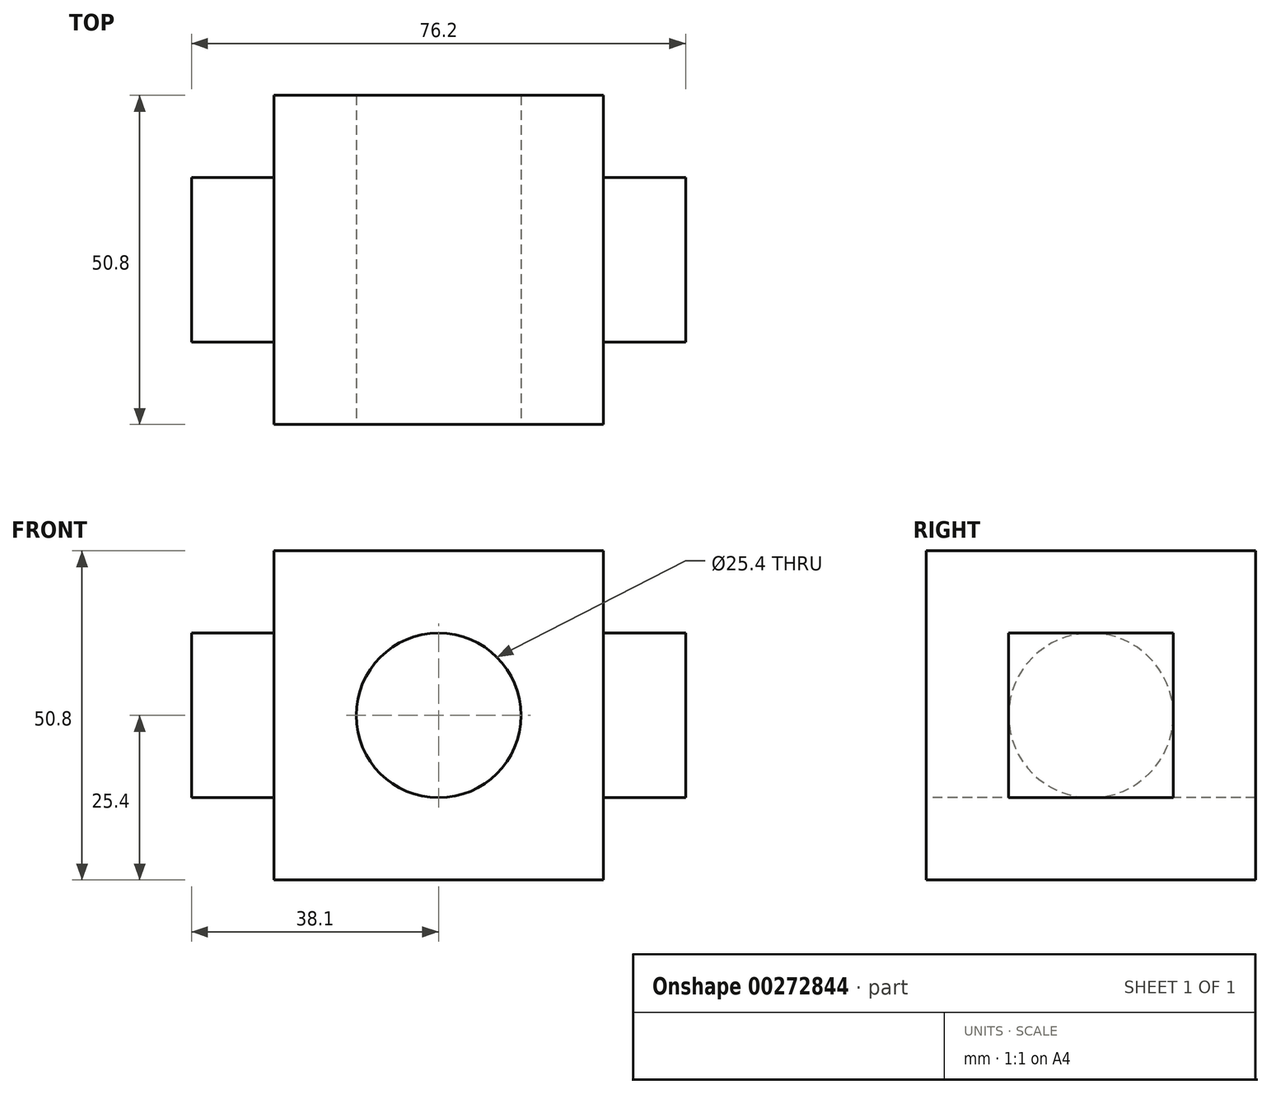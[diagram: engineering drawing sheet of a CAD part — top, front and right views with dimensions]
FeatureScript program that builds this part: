
annotation { "Feature Type Name" : "Feature", "Feature Type Description" : "" }
export const myFeature = defineFeature(function(context is Context, id is Id, definition is map)
    precondition{}
    {
        {
            var Q0;
            Q0=qCreatedBy(makeId("Front.planeOp"),FACE);
            var sketch = newSketch(context, id + "F0", { "sketchPlane" : qUnion([Q0])});
            skLineSegment(sketch, "E0", {"start": v(0, 0) * mm, "end": v(-50.8, 0) * mm});
            skLineSegment(sketch, "E1", {"start": v(-50.8, 0) * mm, "end": v(-50.8, 50.8) * mm});
            skLineSegment(sketch, "E2", {"start": v(-50.8, 50.8) * mm, "end": v(0, 50.8) * mm});
            skLineSegment(sketch, "E3", {"start": v(0, 50.8) * mm, "end": v(0, 0) * mm});
            skSolve(sketch);
        }
        {
            var Q0;
            Q0=makeQuery(id+"F0.imprint","IMPRINT",FACE,{"disambiguationData":[TD([[makeQuery(id+"F0.imprint","IMPRINT",EDGE,{"derivedFrom":sQuery(id+"F0.wireOp",EDGE,"E0")}),-1.0]])]});
            extrude(context, id + "F1", {"entities" : qUnion([Q0]), "depth" : 50.8 * mm});
        }
        {
            var Q0;
            Q0=makeQuery(id+"F1.opExtrude","CAP_FACE",FACE,{"disambiguationData":[OSD([sQuery(id+"F0.wireOp",EDGE,"E0"),sQuery(id+"F0.wireOp",EDGE,"E1"),sQuery(id+"F0.wireOp",EDGE,"E2"),sQuery(id+"F0.wireOp",EDGE,"E3")])],"isStart":false});
            var sketch = newSketch(context, id + "F2", { "sketchPlane" : qUnion([Q0])});
            skCircle(sketch, "E4", {"center": v(-25.4, 25.4) * mm, "radius": 12.7 * mm});
            skSolve(sketch);
        }
        {
            var Q0;
            Q0=makeQuery(id+"F2.imprint","IMPRINT",FACE,{"disambiguationData":[TD([[makeQuery(id+"F2.imprint","IMPRINT",EDGE,{"derivedFrom":sQuery(id+"F2.wireOp",EDGE,"E4")}),1.0]])]});
            extrude(context, id + "F3", {"entities" : qUnion([Q0]), "operationType" : NewBodyOperationType.REMOVE, "oppositeDirection" : true, "depth" : 50.8 * mm});
        }
        {
            var Q0;
            Q0=makeQuery(id+"F1.opExtrude","SWEPT_FACE",FACE,{"disambiguationData":[OSD([sQuery(id+"F0.wireOp",EDGE,"E3")])]});
            var sketch = newSketch(context, id + "F4", { "sketchPlane" : qUnion([Q0])});
            skLineSegment(sketch, "E5.bottom", {"start": v(-38.1, 38.1) * mm, "end": v(-12.7, 38.1) * mm});
            skLineSegment(sketch, "E5.top", {"start": v(-38.1, 12.7) * mm, "end": v(-12.7, 12.7) * mm});
            skLineSegment(sketch, "E5.left", {"start": v(-38.1, 38.1) * mm, "end": v(-38.1, 12.7) * mm});
            skLineSegment(sketch, "E5.right", {"start": v(-12.7, 38.1) * mm, "end": v(-12.7, 12.7) * mm});
            skSolve(sketch);
        }
        {
            var Q0;
            Q0=makeQuery(id+"F4.imprint","IMPRINT",FACE,{"disambiguationData":[TD([[makeQuery(id+"F4.imprint","IMPRINT",EDGE,{"derivedFrom":sQuery(id+"F4.wireOp",EDGE,"E5.bottom")}),-1.0]])]});
            extrude(context, id + "F5", {"entities" : qUnion([Q0]), "operationType" : NewBodyOperationType.ADD, "depth" : 12.7 * mm});
        }
        {
            var Q0;
            Q0=makeQuery(id+"F1.opExtrude","SWEPT_FACE",FACE,{"disambiguationData":[OSD([sQuery(id+"F0.wireOp",EDGE,"E1")])]});
            var sketch = newSketch(context, id + "F6", { "sketchPlane" : qUnion([Q0])});
            skCircle(sketch, "E6", {"center": v(25.4, 25.4) * mm, "radius": 12.7 * mm});
            skSolve(sketch);
        }
        {
            var Q0;
            Q0=makeQuery(id+"F6.imprint","IMPRINT",FACE,{"disambiguationData":[TD([[makeQuery(id+"F6.imprint","IMPRINT",EDGE,{"derivedFrom":sQuery(id+"F6.wireOp",EDGE,"E6")}),1.0]])]});
            extrude(context, id + "F7", {"entities" : qUnion([Q0]), "operationType" : NewBodyOperationType.ADD, "depth" : 12.7 * mm});
        }
    });
